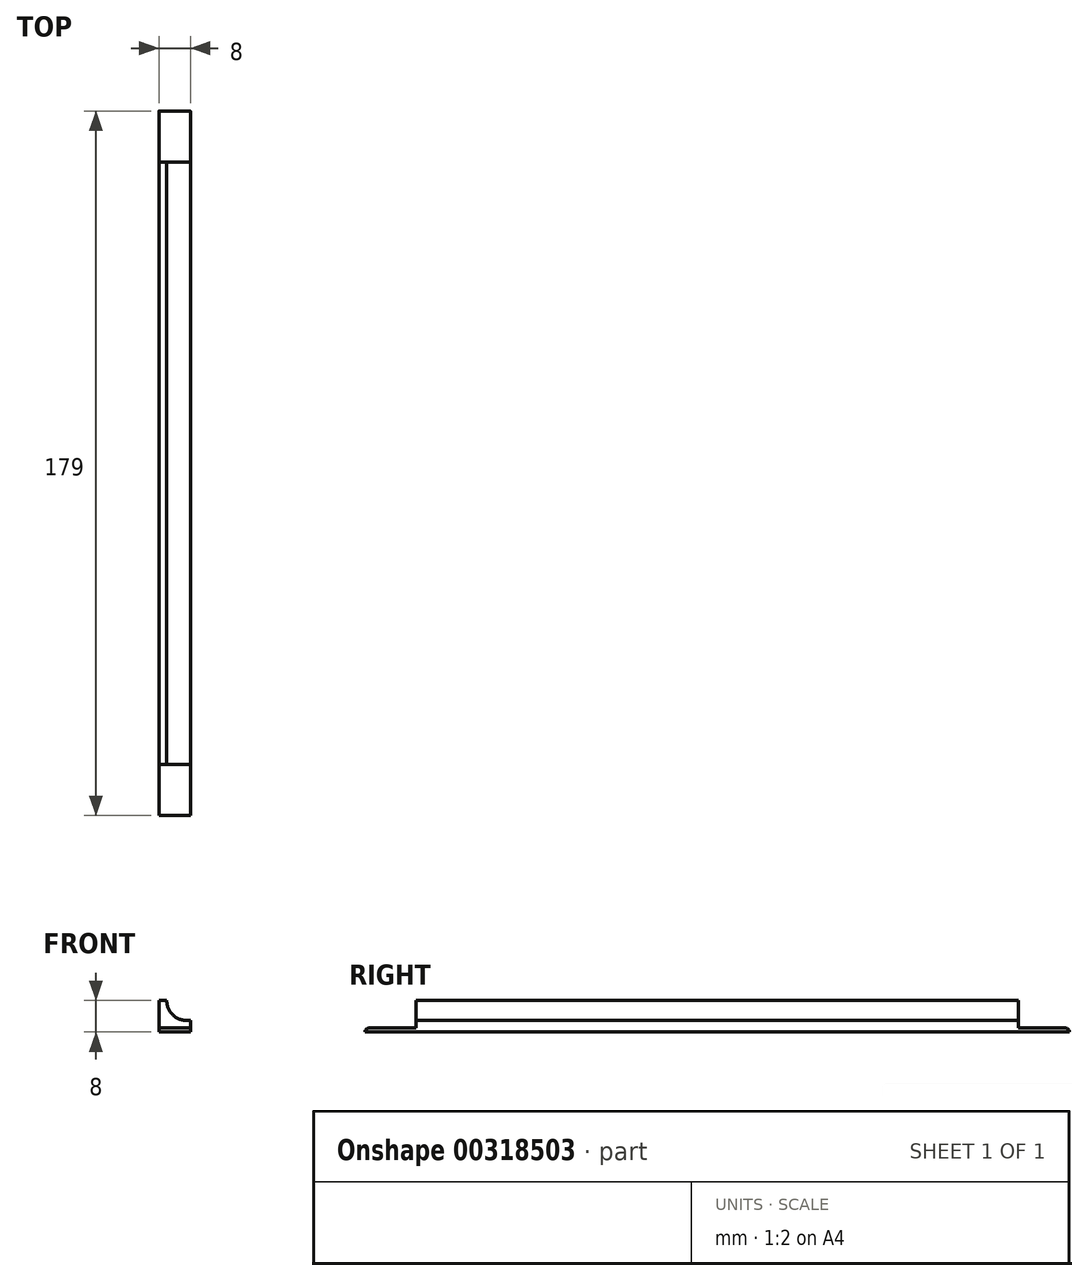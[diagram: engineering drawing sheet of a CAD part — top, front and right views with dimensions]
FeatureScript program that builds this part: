
annotation { "Feature Type Name" : "Feature", "Feature Type Description" : "" }
export const myFeature = defineFeature(function(context is Context, id is Id, definition is map)
    precondition{}
    {
        {
            var Q0;
            Q0=qCreatedBy(makeId("Top.planeOp"),FACE);
            var sketch = newSketch(context, id + "F0", { "sketchPlane" : qUnion([Q0])});
            skLineSegment(sketch, "E0.bottom", {"start": v(4, 76.5) * mm, "end": v(-4, 76.5) * mm});
            skLineSegment(sketch, "E0.top", {"start": v(4, -76.5) * mm, "end": v(-4, -76.5) * mm});
            skLineSegment(sketch, "E0.left", {"start": v(4, 76.5) * mm, "end": v(4, -76.5) * mm});
            skLineSegment(sketch, "E0.right", {"start": v(-4, 76.5) * mm, "end": v(-4, -76.5) * mm});
            skPoint(sketch, "E0.middle", {"position": v(0, 0) * mm});
            skSolve(sketch);
        }
        {
            var Q0;
            Q0 = qSketchRegion(id + "F0", true);
            extrude(context, id + "F1", {"entities" : qUnion([Q0]), "depth" : 7 * mm});
        }
        {
            var Q0;
            Q0=makeQuery(id+"F1.opExtrude","SWEPT_FACE",FACE,{"disambiguationData":[OSD([sQuery(id+"F0.wireOp",EDGE,"E0.top")])]});
            var sketch = newSketch(context, id + "F2", { "sketchPlane" : qUnion([Q0])});
            skLineSegment(sketch, "E1", {"start": v(-4, 7) * mm, "end": v(-2, 7) * mm, "construction": true});
            skLineSegment(sketch, "E2", {"start": v(4, 0) * mm, "end": v(4, 2) * mm, "construction": true});
            skLineSegment(sketch, "E3", {"start": v(-4, 0) * mm, "end": v(0, 2.98) * mm, "construction": true});
            skArc(sketch, "E4", {"start": v(-2, 7) * mm, "mid": v(-0.16, 3.1) * mm, "end": v(4, 2) * mm});
            skSolve(sketch);
        }
        {
            var Q0;
            {var subQ0=sQuery(id+"F2.wireOp",EDGE,"E4");Q0=makeQuery(id+"F2.imprint","IMPRINT",FACE,{"disambiguationData":[TD([[makeQuery(id+"F2.imprint","IMPRINT",EDGE,{"derivedFrom":subQ0}),1.0]])]});}
            extrude(context, id + "F3", {"entities" : qUnion([Q0]), "operationType" : NewBodyOperationType.REMOVE, "oppositeDirection" : true, "depth" : 160 * mm});
        }
        {
            var Q0;
            Q0=makeQuery(id+"F1.opExtrude","CAP_FACE",FACE,{"disambiguationData":[OSD([sQuery(id+"F0.wireOp",EDGE,"E0.bottom"),sQuery(id+"F0.wireOp",EDGE,"E0.top"),sQuery(id+"F0.wireOp",EDGE,"E0.left"),sQuery(id+"F0.wireOp",EDGE,"E0.right")])],"isStart":true});
            var sketch = newSketch(context, id + "F4", { "sketchPlane" : qUnion([Q0])});
            skLineSegment(sketch, "E5.bottom", {"start": v(4, 89.5) * mm, "end": v(-4, 89.5) * mm});
            skLineSegment(sketch, "E5.top", {"start": v(4, -89.5) * mm, "end": v(-4, -89.5) * mm});
            skLineSegment(sketch, "E5.left", {"start": v(4, 89.5) * mm, "end": v(4, -89.5) * mm});
            skLineSegment(sketch, "E5.right", {"start": v(-4, 89.5) * mm, "end": v(-4, -89.5) * mm});
            skPoint(sketch, "E5.middle", {"position": v(0, 0) * mm});
            skSolve(sketch);
        }
        {
            var Q0;
            Q0 = qSketchRegion(id + "F4", true);
            extrude(context, id + "F5", {"entities" : qUnion([Q0]), "operationType" : NewBodyOperationType.ADD, "depth" : 1 * mm});
        }
        {
            var Q0;
            Q0=makeQuery(id+"F5.opExtrude","CAP_EDGE",EDGE,{"disambiguationData":[OSD([sQuery(id+"F4.wireOp",EDGE,"E5.bottom")])],"isStart":true});
            var Q1;
            Q1=makeQuery(id+"F5.opExtrude","CAP_EDGE",EDGE,{"disambiguationData":[OSD([sQuery(id+"F4.wireOp",EDGE,"E5.top")])],"isStart":true});
            fillet(context, id + "F6", {"entities" : qUnion([Q0, Q1]), "radius" : 1 * mm, "tangentPropagation" : true, "allowEdgeOverflow" : false});
        }
    });
